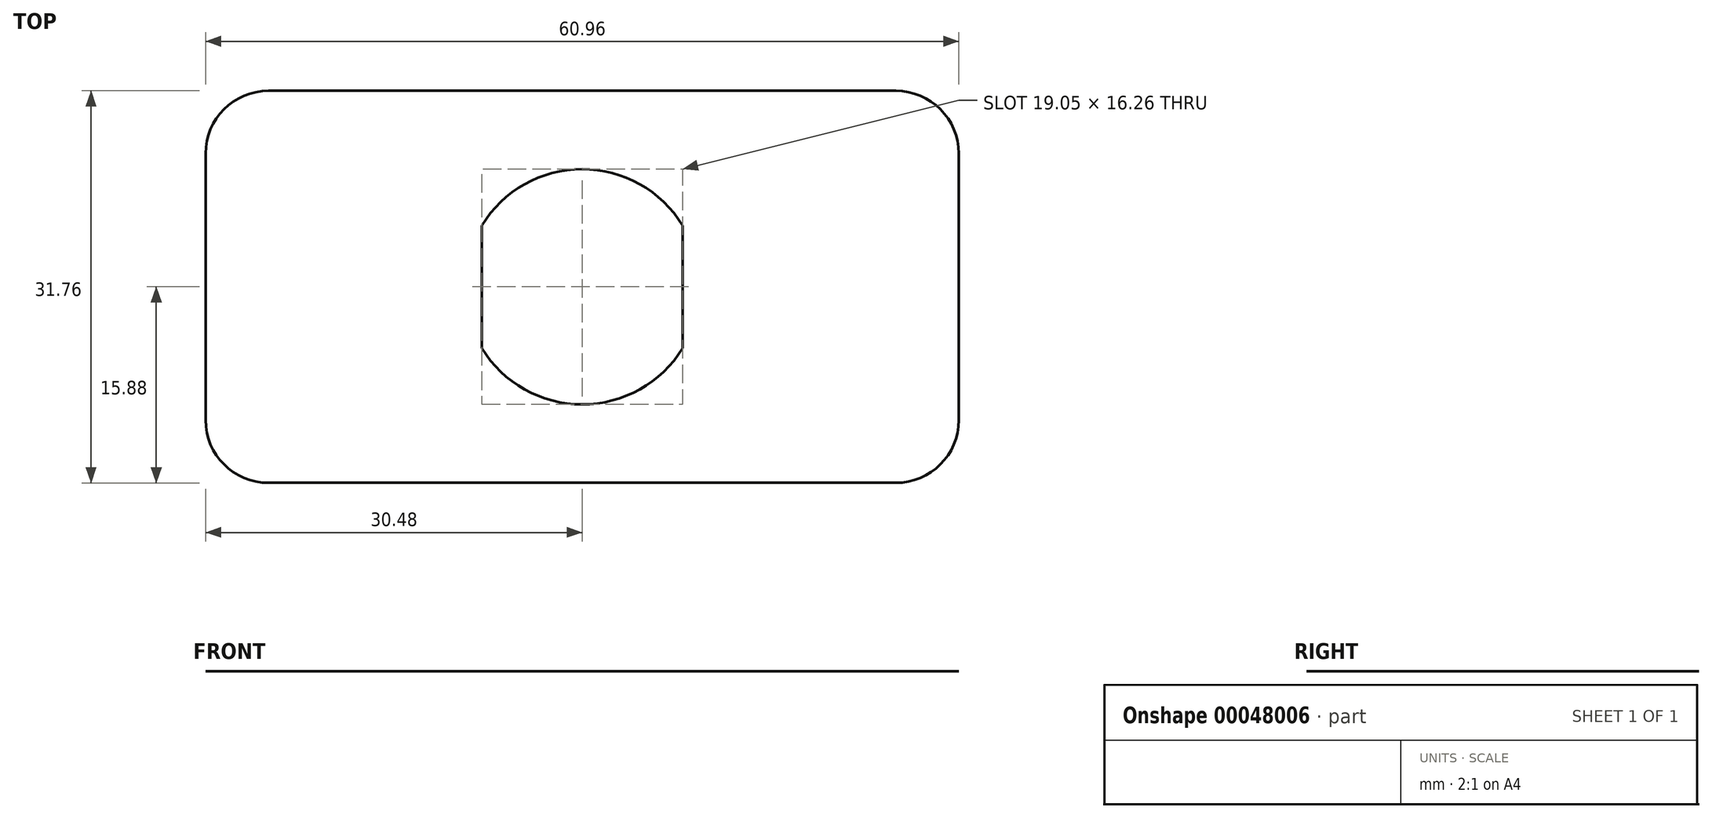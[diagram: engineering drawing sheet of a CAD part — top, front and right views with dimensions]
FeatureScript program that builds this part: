
annotation { "Feature Type Name" : "Feature", "Feature Type Description" : "" }
export const myFeature = defineFeature(function(context is Context, id is Id, definition is map)
    precondition{}
    {
        {
            var Q0;
            Q0=qCreatedBy(makeId("Top.planeOp"),FACE);
            var sketch = newSketch(context, id + "F0", { "sketchPlane" : qUnion([Q0])});
            skLineSegment(sketch, "E0.bottom", {"start": v(-30.48, 15.88) * mm, "end": v(30.48, 15.88) * mm});
            skLineSegment(sketch, "E0.top", {"start": v(-30.48, -15.88) * mm, "end": v(30.48, -15.88) * mm});
            skLineSegment(sketch, "E0.left", {"start": v(-30.48, 15.88) * mm, "end": v(-30.48, -15.88) * mm});
            skLineSegment(sketch, "E0.right", {"start": v(30.48, 15.88) * mm, "end": v(30.48, -15.88) * mm});
            skLineSegment(sketch, "E1", {"start": v(0, 15.88) * mm, "end": v(0, -15.88) * mm, "construction": true});
            skLineSegment(sketch, "E2", {"start": v(-30.48, 0) * mm, "end": v(30.48, 0) * mm, "construction": true});
            skPoint(sketch, "E3", {"position": v(0, 0) * mm});
            skLineSegment(sketch, "E4.bottom", {"start": v(-8.13, 4.97) * mm, "end": v(8.13, 4.97) * mm});
            skLineSegment(sketch, "E4.top", {"start": v(-8.13, -4.97) * mm, "end": v(8.13, -4.97) * mm});
            skLineSegment(sketch, "E4.left", {"start": v(-8.13, 4.97) * mm, "end": v(-8.13, -4.97) * mm});
            skLineSegment(sketch, "E4.right", {"start": v(8.13, 4.97) * mm, "end": v(8.13, -4.97) * mm});
            skPoint(sketch, "E5", {"position": v(-8.13, 0) * mm});
            skArc(sketch, "E6", {"start": v(-8.13, 4.97) * mm, "mid": v(0, 9.53) * mm, "end": v(8.13, 4.97) * mm});
            skArc(sketch, "E7", {"start": v(8.13, -4.97) * mm, "mid": v(0, -9.53) * mm, "end": v(-8.13, -4.97) * mm});
            skSolve(sketch);
        }
        {
            var Q0;
            Q0 = qSketchRegion(id + "F0", true);
            extrude(context, id + "F1", {"entities" : qUnion([Q0]), "depth" : 1 / 203.2 * mm});
        }
        {
            var Q0;
            Q0=makeQuery(id+"F1.opExtrude","SWEPT_EDGE",EDGE,{"disambiguationData":[OSD([sQuery(id+"F0.wireOp",EDGE,"E0.bottom"),sQuery(id+"F0.wireOp",EDGE,"E0.left")])]});
            var Q1;
            Q1=makeQuery(id+"F1.opExtrude","SWEPT_EDGE",EDGE,{"disambiguationData":[OSD([sQuery(id+"F0.wireOp",EDGE,"E0.bottom"),sQuery(id+"F0.wireOp",EDGE,"E0.right")])]});
            var Q2;
            Q2=makeQuery(id+"F1.opExtrude","SWEPT_EDGE",EDGE,{"disambiguationData":[OSD([sQuery(id+"F0.wireOp",EDGE,"E0.top"),sQuery(id+"F0.wireOp",EDGE,"E0.left")])]});
            var Q3;
            Q3=makeQuery(id+"F1.opExtrude","SWEPT_EDGE",EDGE,{"disambiguationData":[OSD([sQuery(id+"F0.wireOp",EDGE,"E0.top"),sQuery(id+"F0.wireOp",EDGE,"E0.right")])]});
            fillet(context, id + "F2", {"entities" : qUnion([Q0, Q1, Q2, Q3]), "radius" : 5.08 * mm, "tangentPropagation" : true, "allowEdgeOverflow" : false});
        }
    });
